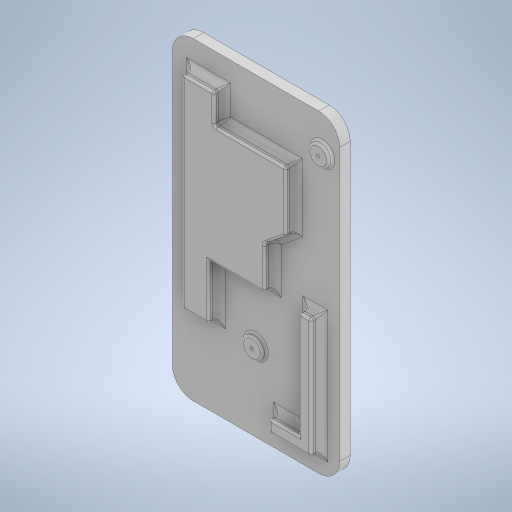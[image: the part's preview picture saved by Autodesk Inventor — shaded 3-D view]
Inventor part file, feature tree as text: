
AUTODESK INVENTOR PART (.ipt)
format: ipt  version: 2024.3 (Build 283343000, 343)  size: 406,016 bytes
history: native  units: mm
features: fillet x8, extrude x4, sketch x4, other x3
ambient origin geometry x8: Origin, YZ Plane, XZ Plane, XY Plane, X Axis, Y Axis, Z Axis, Center Point
bodies: Solido1 (feature_tree)
feature tree (19):
  extrude  "Estrusione1"  Depth=1.5mm
  extrude  "Estrusione2"  Depth=0.8mm
  fillet  "Raccordo1"  Radius=0.05mm
  fillet  "Raccordo2"  Radius=0.05mm
  fillet  "Raccordo3"  Radius=0.03mm
  fillet  "Raccordo4"  Radius=0.03mm
  fillet  "Raccordo5"  Radius=0.01mm
  extrude  "Estrusione3"  Depth=0.01mm
  fillet  "Raccordo6"  Radius=0.01mm
  extrude  "Estrusione4"  Depth=0.1mm
  fillet  "Raccordo7"  Radius=0.1mm
  fillet  "Raccordo8"  Radius=0.02mm
  sketch  "Schizzo1"
  sketch  "Schizzo2"
  other  "Linea chiusa proiettata1"
  sketch  "Schizzo3"
  sketch  "Schizzo4"
  other  "Linea chiusa proiettata2"
  other  "Linea chiusa proiettata3"
